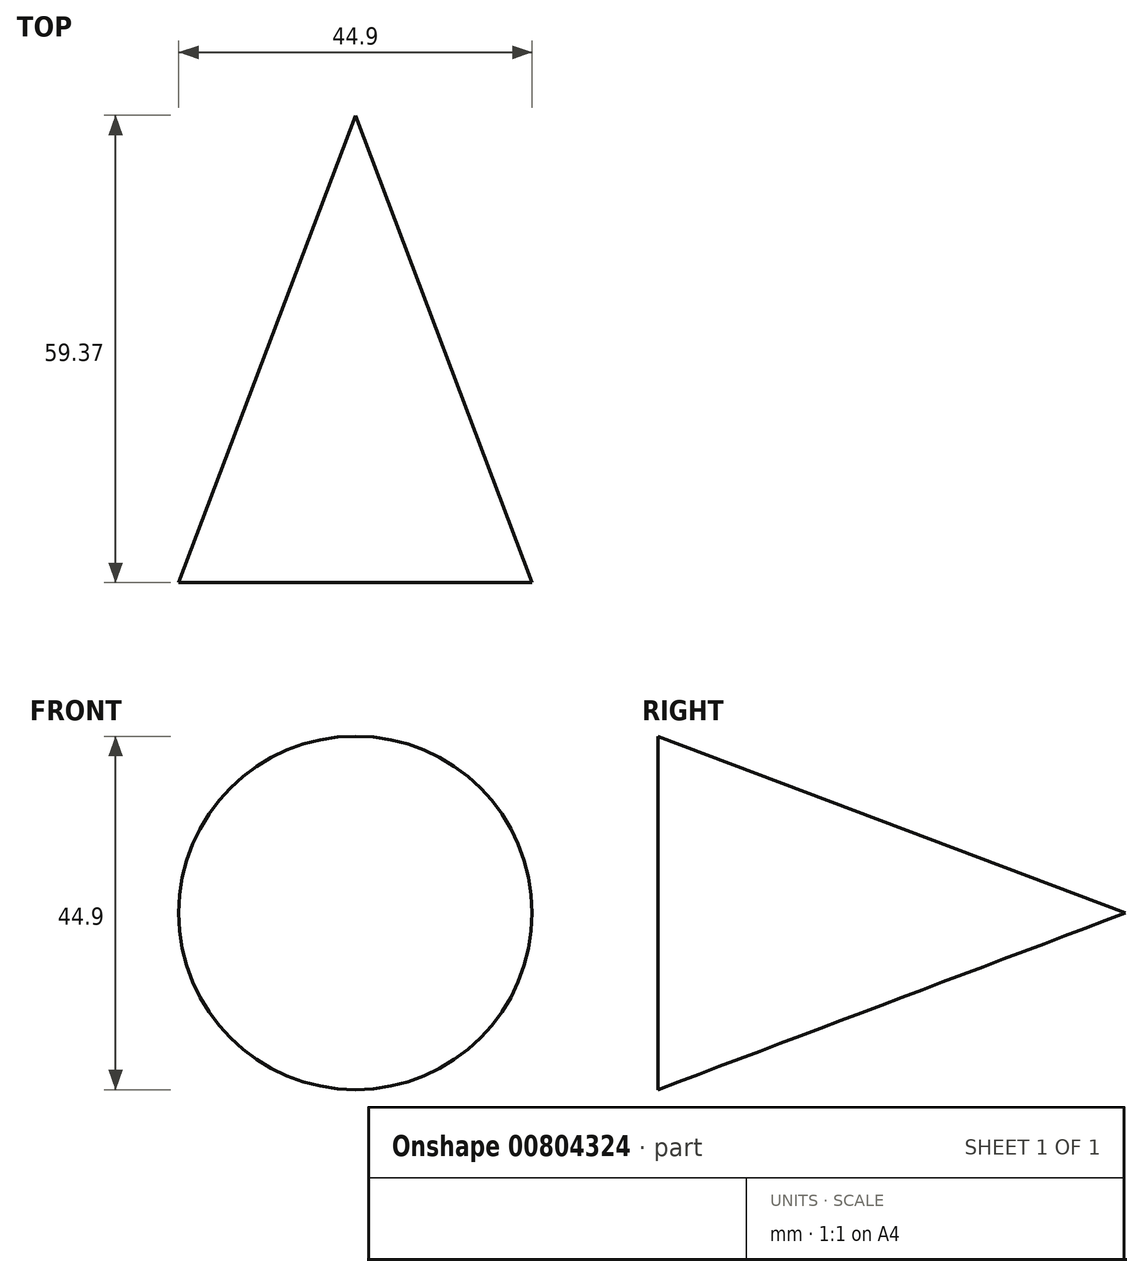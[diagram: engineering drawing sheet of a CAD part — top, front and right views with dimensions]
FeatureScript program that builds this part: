
annotation { "Feature Type Name" : "Feature", "Feature Type Description" : "" }
export const myFeature = defineFeature(function(context is Context, id is Id, definition is map)
    precondition{}
    {
        {
            var Q0;
            Q0=qCreatedBy(makeId("Top.planeOp"),FACE);
            var sketch = newSketch(context, id + "F0", { "sketchPlane" : qUnion([Q0])});
            skLineSegment(sketch, "E0", {"start": v(0, 0) * mm, "end": v(0, 59.37) * mm});
            skLineSegment(sketch, "E1", {"start": v(0, 0) * mm, "end": v(22.45, 0) * mm});
            skLineSegment(sketch, "E2", {"start": v(22.45, 0) * mm, "end": v(0, 59.37) * mm});
            skSolve(sketch);
        }
        {
            var Q0;
            Q0=makeQuery(id+"F0.imprint","IMPRINT",FACE,{"disambiguationData":[TD([[makeQuery(id+"F0.imprint","IMPRINT",EDGE,{"derivedFrom":sQuery(id+"F0.wireOp",EDGE,"E0")}),-1.0]])]});
            var Q1;
            Q1=sQuery(id+"F0.wireOp",EDGE,"E0");
            revolve(context, id + "F1", {"surfaceOperationType" : NewSurfaceOperationType.NEW, "entities" : qUnion([Q0]), "axis" : qUnion([Q1]), "revolveType" : RevolveType.FULL});
        }
    });
